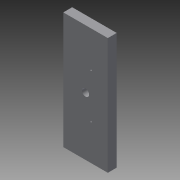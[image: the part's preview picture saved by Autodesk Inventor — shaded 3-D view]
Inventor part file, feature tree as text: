
AUTODESK INVENTOR PART (.ipt)
format: ipt  version: 2015 (Build 190159000, 159)  size: 77,824 bytes
history: native  units: mm
features: extrude x2, sketch x1
ambient origin geometry x8: Origin, YZ Plane, XZ Plane, XY Plane, X Axis, Y Axis, Z Axis, Center Point
bodies: Solid1 (feature_tree)
feature tree (3):
  sketch  "Sketch1"  dims[d0=50.0mm d1=131.0mm d2=10.0mm d3=0.0mm d4=8.0mm d10=2.0mm d11=10.0mm d12=0.0mm]
  extrude  "Extrusion1"  Depth=131.0mm
  extrude  "Extrusion2"  Depth=10.0mm TaperAngle=0.0deg
